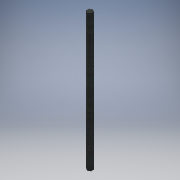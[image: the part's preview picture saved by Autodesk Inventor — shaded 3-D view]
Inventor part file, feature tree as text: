
AUTODESK INVENTOR PART (.ipt)
format: ipt  version: 2016 (Build 200138000, 138)  size: 93,696 bytes
history: native  units: in
note: dims shown in document units (in); Inventor stores cm internally (conversion verified against a paired STEP export)
features: extrude x1, sketch x1
ambient origin geometry x8: Origin, YZ Plane, XZ Plane, XY Plane, X Axis, Y Axis, Z Axis, Center Point
bodies: Solid1 (feature_tree)
feature tree (2):
  extrude  "Extrusion1"  Depth=14.0in TaperAngle=0.0deg
  sketch  "Sketch1"  dims[d0=0.5in d1=14.0in d2=0.0in]
